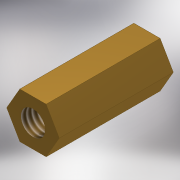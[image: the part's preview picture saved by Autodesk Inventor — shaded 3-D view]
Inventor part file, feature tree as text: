
AUTODESK INVENTOR PART (.ipt)
format: ipt  version: 2018 (Build 220112000, 112)  size: 110,080 bytes
history: native  units: mm
features: sketch x2, extrude x1, hole x1
ambient origin geometry x8: Origin, YZ Plane, XZ Plane, XY Plane, X Axis, Y Axis, Z Axis, Center Point
bodies: Solid1 (feature_tree)
feature tree (4):
  extrude  "Extrusion1"  Depth=15.0mm TaperAngle=0.0deg
  hole  "Hole1"  [1 undecoded]
  sketch  "Sketch1"  dims[d0=3.0mm d1=15.0mm d2=0.0mm]
  sketch  "Sketch2"  dims[d3=3.242mm d4=8.0mm d5=4.0mm d6=2.0mm d7=90.0deg d8=8.0mm d9=20.594885mm]
note: 1 required parameter value undecoded (feature->parameter linkage not recoverable at this tier; creation-order binding heuristic only, values carry confidence <= 0.55)
